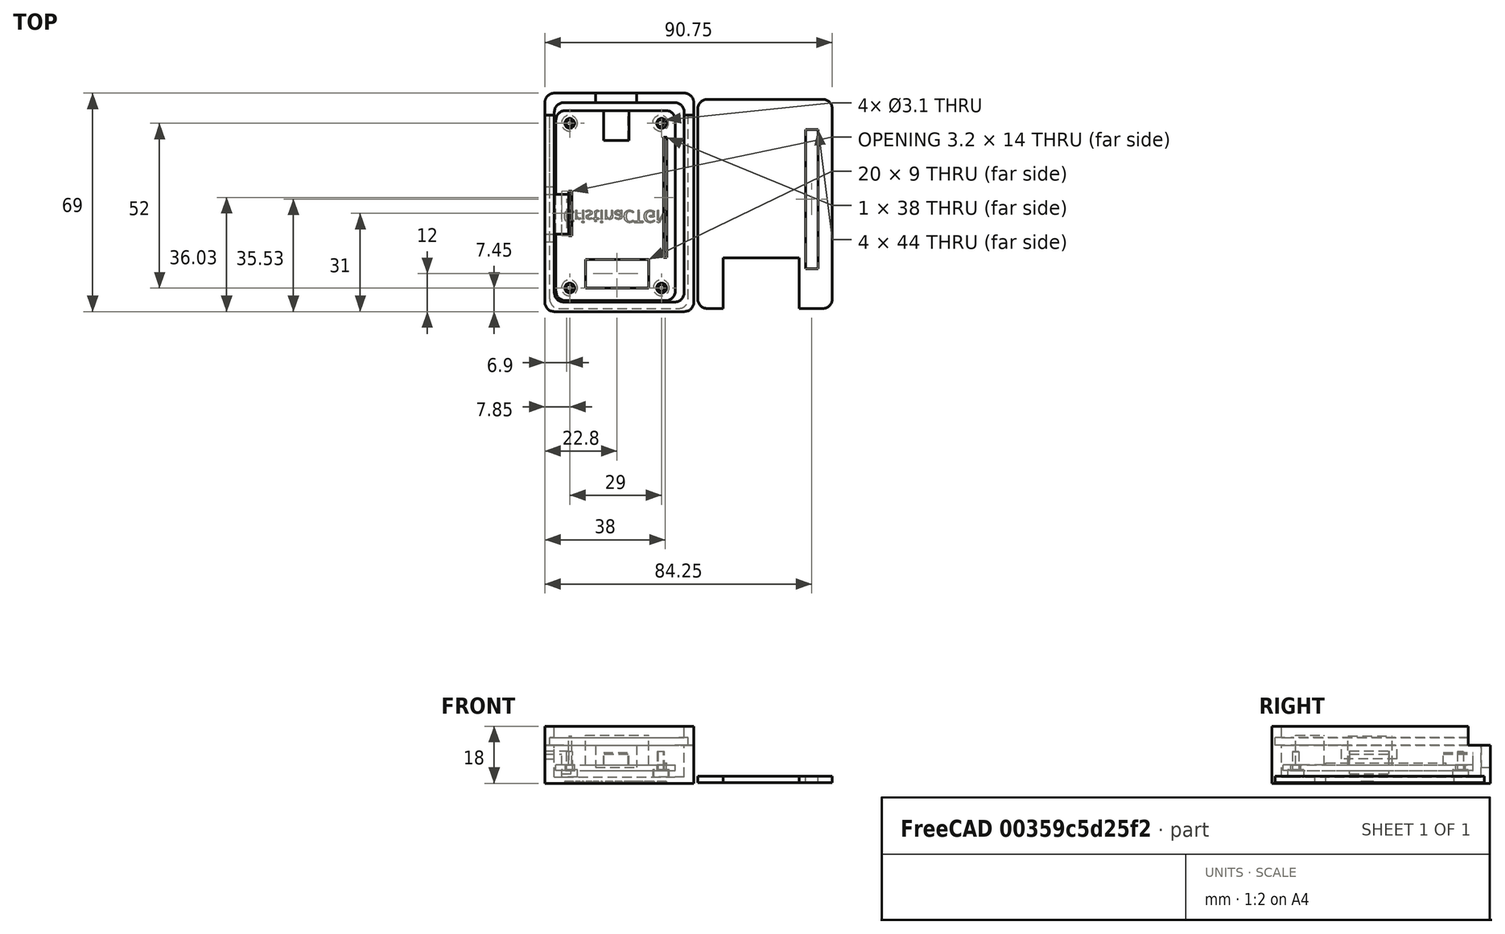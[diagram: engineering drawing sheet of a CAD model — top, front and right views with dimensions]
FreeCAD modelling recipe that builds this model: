
FCSTD DOCUMENT  (FreeCAD 0.21R33668 +26 (Git))
Label: busPiratev3_iteracion2
License: All rights reserved
LicenseURL: https://en.wikipedia.org/wiki/All_rights_reserved
objects: Part::Box×17, Part::Cut×14, Part::Cylinder×12, Part::Fillet×11, Part::MultiFuse×6, Part::Part2DObjectPython×1, Part::Extrusion×1
note: 62 computed .brp shape members not serialized (recipe doc carries the construction recipe); baked Part::Feature solids carry a one-line shape summary decoded from their .brp

FEATURE [Part::Box] Box  label="Placa"
  AttacherType = Attacher::AttachEngine3D
  Height = 1.8
  Length = 37.7
  Width = 60
FEATURE [Part::Box] Box001  label="Conector"
  AttacherType = Attacher::AttachEngine3D
  Height = 11.19
  Length = 20
  Placement = pos=(9.3,4,0) rot=(0,0,1;0rad)
  Width = 9
FEATURE [Part::MultiFuse] Fusion
  Shapes = -> [Box001,Box]
FEATURE [Part::Cylinder] Cylinder  label="hueco de tornillo 1"
  Angle = 360
  AttacherType = Attacher::AttachEngine3D
  FirstAngle = 0
  Height = 10
  Placement = pos=(4.35,3.95,0) rot=(0,0,1;0rad)
  Radius = 1.55
  SecondAngle = 0
FEATURE [Part::Cylinder] Cylinder001  label="hueco de tornillo 002"
  Angle = 360
  AttacherType = Attacher::AttachEngine3D
  FirstAngle = 0
  Height = 10
  Placement = pos=(33.35,3.95,0) rot=(0,0,1;0rad)
  Radius = 1.55
  SecondAngle = 0
FEATURE [Part::Cylinder] Cylinder002  label="hueco de tornillo 003"
  Angle = 360
  AttacherType = Attacher::AttachEngine3D
  FirstAngle = 0
  Height = 10
  Placement = pos=(4.35,55.95,0) rot=(0,0,1;0rad)
  Radius = 1.55
  SecondAngle = 0
FEATURE [Part::Cylinder] Cylinder003  label="hueco de tornillo 004"
  Angle = 360
  AttacherType = Attacher::AttachEngine3D
  FirstAngle = 0
  Height = 10
  Placement = pos=(33.35,55.95,0) rot=(0,0,1;0rad)
  Radius = 1.55
  SecondAngle = 0
FEATURE [Part::Cut] Cut
  Base = -> Fusion
  Tool = -> Cylinder002
FEATURE [Part::Cut] Cut001
  Base = -> Cut
  Tool = -> Cylinder
FEATURE [Part::Cut] Cut002
  Base = -> Cut001
  Tool = -> Cylinder003
FEATURE [Part::Cut] Cut003
  Base = -> Cut002
  Tool = -> Cylinder001
FEATURE [Part::Fillet] Fillet
  Base = -> Cut003
  Edges = 1 edges r=3: [Edge13]
FEATURE [Part::Fillet] Fillet001
  Base = -> Fillet
  Edges = 1 edges r=3: [Edge22]
FEATURE [Part::Fillet] Fillet002
  Base = -> Fillet001
  Edges = 1 edges r=3: [Edge23]
FEATURE [Part::Fillet] Fillet003
  Base = -> Fillet002
  Edges = 1 edges r=3: [Edge23]
FEATURE [Part::Box] Box002  label="Cubo"
  AttacherType = Attacher::AttachEngine3D
  Height = 7.3
  Length = 8.3
  Placement = pos=(-3.5,21,-1) rot=(0,0,1;0rad)
  Width = 12.5
FEATURE [Part::Box] Box003  label="Cubo001"
  AttacherType = Attacher::AttachEngine3D
  Height = 6.3
  Length = 5.3
  Placement = pos=(-3.5,21,-1) rot=(0,0,1;0rad)
  Width = 12.5
FEATURE [Part::Cut] Cut004  label="Conector001"
  Base = -> Box002
  Tool = -> Box003
FEATURE [Part::MultiFuse] Fusion001
  Shapes = -> [Fillet003,Cut004]
FEATURE [Part::Box] Box004  label="Cubo002"
  AttacherType = Attacher::AttachEngine3D
  Height = 5.7
  Length = 8
  Placement = pos=(15,50.6,0) rot=(0,0,1;0rad)
  Width = 9.4
FEATURE [Part::Box] Box005  label="Cubo003"
  AttacherType = Attacher::AttachEngine3D
  Height = 3.5
  Length = 7.6
  Placement = pos=(15.2,50.6,1.8) rot=(0,0,1;0rad)
  Width = 9.4
FEATURE [Part::Cut] Cut005
  Base = -> Box004
  Tool = -> Box005
FEATURE [Part::MultiFuse] Fusion002
  Shapes = -> [Fusion001,Cut005]
FEATURE [Part::Box] Box006  label="Leds"
  AttacherType = Attacher::AttachEngine3D
  Height = 2.4
  Length = 1
  Placement = pos=(34,13.53,0) rot=(0,0,1;0rad)
  Width = 38
FEATURE [Part::MultiFuse] Fusion003
  Placement = pos=(-95.5,3.5,4) rot=(0,0,1;0rad)
  Shapes = -> [Fusion002,Box006]
FEATURE [Part::Box] Box007  label="Cubo004"
  AttacherType = Attacher::AttachEngine3D
  Height = 18
  Length = 47
  Width = 69
FEATURE [Part::Box] Box008  label="Cubo005"
  AttacherType = Attacher::AttachEngine3D
  Height = 16
  Length = 41
  Placement = pos=(3,3,2) rot=(0,0,1;0rad)
  Width = 63
FEATURE [Part::Cut] Cut006
  Base = -> Box007
  Tool = -> Box008
FEATURE [Part::Cylinder] Cylinder004  label="Cilindro"
  Angle = 360
  AttacherType = Attacher::AttachEngine3D
  FirstAngle = 0
  Height = 10
  Placement = pos=(7.75,7.5,0) rot=(0,0,1;0rad)
  Radius = 1
  SecondAngle = 0
FEATURE [Part::Cylinder] Cylinder005  label="Cilindro001"
  Angle = 360
  AttacherType = Attacher::AttachEngine3D
  FirstAngle = 0
  Height = 10
  Placement = pos=(36.75,7.5,0) rot=(0,0,1;0rad)
  Radius = 1
  SecondAngle = 0
FEATURE [Part::Cylinder] Cylinder006  label="Cilindro002"
  Angle = 360
  AttacherType = Attacher::AttachEngine3D
  FirstAngle = 0
  Height = 10
  Placement = pos=(7.75,59.5,0) rot=(0,0,1;0rad)
  Radius = 1
  SecondAngle = 0
FEATURE [Part::Cylinder] Cylinder007  label="Cilindro003"
  Angle = 360
  AttacherType = Attacher::AttachEngine3D
  FirstAngle = 0
  Height = 10
  Placement = pos=(36.5,59.5,0) rot=(0,0,1;0rad)
  Radius = 1
  SecondAngle = 0
FEATURE [Part::Cylinder] Cylinder008  label="Cilindro004"
  Angle = 360
  AttacherType = Attacher::AttachEngine3D
  FirstAngle = 0
  Height = 3.3
  Placement = pos=(36.5,59.5,1) rot=(0,0,1;0rad)
  Radius = 2.5
  SecondAngle = 0
FEATURE [Part::Cylinder] Cylinder009  label="Cilindro005"
  Angle = 360
  AttacherType = Attacher::AttachEngine3D
  FirstAngle = 0
  Height = 3.3
  Placement = pos=(7.75,59.5,1) rot=(0,0,1;0rad)
  Radius = 2.5
  SecondAngle = 0
FEATURE [Part::Cylinder] Cylinder010  label="Cilindro006"
  Angle = 360
  AttacherType = Attacher::AttachEngine3D
  FirstAngle = 0
  Height = 3.3
  Placement = pos=(7.75,7.5,1) rot=(0,0,1;0rad)
  Radius = 2.5
  SecondAngle = 0
FEATURE [Part::Cylinder] Cylinder011  label="Cilindro007"
  Angle = 360
  AttacherType = Attacher::AttachEngine3D
  FirstAngle = 0
  Height = 3.3
  Placement = pos=(36.75,7.5,1) rot=(0,0,1;0rad)
  Radius = 2.5
  SecondAngle = 0
FEATURE [Part::Fillet] Fillet004
  Base = -> Cut006
  Edges = 1 edges r=3: [Edge6]
FEATURE [Part::Fillet] Fillet005
  Base = -> Fillet004
  Edges = 1 edges r=3: [Edge24]
FEATURE [Part::Fillet] Fillet006
  Base = -> Fillet005
  Edges = 6 edges r=3: [Edge12,Edge16,Edge19,Edge22,Edge26,Edge29]
FEATURE [Part::Box] Box009  label="Cubo006"
  AttacherType = Attacher::AttachEngine3D
  Height = 2.5
  Length = 43.75
  Placement = pos=(1.5,0,21) rot=(0,0,1;0rad)
  Width = 70
FEATURE [Part::Fillet] Fillet007
  Base = -> Box009
  Edges = 3 edges r=3: [Edge1,Edge5,Edge7]
FEATURE [Part::Fillet] Fillet008
  Base = -> Fillet007
  Edges = 1 edges r=3: [Edge4]
  Placement = pos=(0,1,-9) rot=(0,0,1;0rad)
FEATURE [Part::Box] Box010  label="Cubo007"
  AttacherType = Attacher::AttachEngine3D
  Height = 2
  Length = 42.5
  Placement = pos=(1,1,21) rot=(0,0,1;0rad)
  Width = 66
FEATURE [Part::Fillet] Fillet009
  Base = -> Box010
  Edges = 3 edges r=3: [Edge1,Edge5,Edge7]
FEATURE [Part::Fillet] Fillet010
  Base = -> Fillet009
  Edges = 1 edges r=3: [Edge4]
  Placement = pos=(0,0,-10) rot=(0,0,1;0rad)
FEATURE [Part::Box] Box011  label="Cubo008"
  AttacherType = Attacher::AttachEngine3D
  Height = 3
  Length = 24
  Placement = pos=(9,0,10.5) rot=(0,0,1;0rad)
  Width = 17
FEATURE [Part::Cut] Cut007
  Base = -> Fillet010
  Tool = -> Box011
FEATURE [Part::Box] Box012  label="Leds001"
  AttacherType = Attacher::AttachEngine3D
  Height = 3.4
  Length = 4
  Placement = pos=(35,13.53,10) rot=(0,0,1;0rad)
  Width = 44
FEATURE [Part::Cut] Cut008
  Base = -> Cut007
  Placement = pos=(47.25,0,-10.75) rot=(0,0,1;0rad)
  Tool = -> Box012
FEATURE [Part::Box] Box013  label="Cubo009"
  AttacherType = Attacher::AttachEngine3D
  Height = 4.25
  Length = 4
  Placement = pos=(0,22,7.75) rot=(0,0,1;0rad)
  Width = 17.5
FEATURE [Part::Cut] Cut009
  Base = -> Fillet006
  Tool = -> Box013
FEATURE [Part::Box] Box014  label="Cubo010"
  AttacherType = Attacher::AttachEngine3D
  Height = 7.25
  Length = 13
  Placement = pos=(16,59,5) rot=(0,0,1;0rad)
  Width = 13
FEATURE [Part::Cut] Cut010
  Base = -> Cut009
  Tool = -> Box014
FEATURE [Part::MultiFuse] Fusion004
  Shapes = -> [Cut010,Cylinder008,Cylinder007,Cylinder011,Cylinder005,Cylinder010,Cylinder004,Cylinder006,Cylinder009]
FEATURE [Part::Cut] Cut011
  Base = -> Fusion004
  Tool = -> Fillet008
FEATURE [Part::Box] Box015  label="Cubo011"
  AttacherType = Attacher::AttachEngine3D
  Height = 11
  Length = 1
  Placement = pos=(-91.5,24,4) rot=(0,0,1;0rad)
  Width = 14
FEATURE [Part::MultiFuse] Fusion005
  Placement = pos=(99,0,0) rot=(0,0,1;0rad)
  Shapes = -> [Fusion003,Box015]
FEATURE [Part::Box] Box016  label="Cubo012"
  AttacherType = Attacher::AttachEngine3D
  Height = 8
  Length = 49
  Placement = pos=(0,62,12) rot=(0,0,1;0rad)
  Width = 13
FEATURE [Part::Cut] Cut012
  Base = -> Cut011
  Tool = -> Box016
FEATURE [Part::Part2DObjectPython] ShapeString  # Draft 2D object (typed FeaturePython)
  FontFile = <path>
  MakeFace = true
  Placement = pos=(-391.07,0,-231.64) rot=(0,0,1;0rad)
  Size = 5
  String = CristinaCTGN
  Tracking = 0
FEATURE [Part::Extrusion] Extrude
  Base = -> ShapeString
  Dir = (0,0,1)
  DirMode = 2
  FaceMakerClass = Part::FaceMakerBullseye
  LengthFwd = 1
  LengthRev = 0
  Placement = pos=(397,32,-231) rot=(1,0,0;3.14159rad)
  Solid = false
  Symmetric = false
FEATURE [Part::Cut] Cut013
  Base = -> Cut012
  Tool = -> Extrude
note: 1 file-system path scrubbed to <path> (originals preserved in the JSON sidecar)
